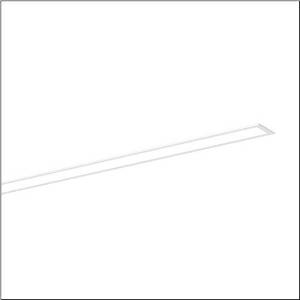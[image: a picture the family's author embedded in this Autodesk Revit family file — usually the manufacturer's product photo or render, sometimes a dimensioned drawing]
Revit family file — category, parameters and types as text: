
# Revit family: silica_r__21_51mx10tbt2w_f160
name_source: partatom
category: Lighting Fixtures
units: mm (PartAtom-declared; Revit-internal decimal feet)

## family parameters
Cut with Voids When Loaded = No
Host = Face
Light Source = No
Part Type = Normal
Room Calculation Point = No
Round Connector Dimension = Use Diameter
Shared = No

## types (1)
- --- (1 x LED, 3000 lm, 25.6 W, 6500K)
    Apparent Load = 26 VA
    CIE Flux Codes = 48 79 96 100 100
    Color Rendering = 80
    Color Temperature = 6500K
    Default Elevation = 1800 mm
    Description = Silica® 21, office luminaire, primary optical cover: cover, of PMMA, opal, light emission: direct distribution, primary light characteristic: symmetric, installation type: recessed, LED, rated luminous flux: 3.000lm, luminous efficacy: 112lm/W, light colour: 8tw, colour temperature: 2700..6500K, control gear: DALI DT8, with terminal, 3+2-pole, max. 2.5mm², mains connection: 220..240V, AC, 50/60Hz, rated input power: 26.9W, luminaire housing, of aluminium, traffic white (RAL 9016), length: 1.504mm, width: 77mm, height: 53mm, protection rating (complete): IP20, insulation class (complete): insulation class I (protective earthing), certification: CE, ENEC, VDE, permissible operating ambient temperature: 0..+35°C, standard: EN 50419, packaging unit: 1 piece
    Height = 0 mm  [stored 0 ft]
    Lamp = 1 x LED
    Lamp Light Flux = 3000 lm
    Lamp Power = 25.6 W
    Lamp count = 1
    Length = 1527 mm
    Luminous efficacy = 117 lm/W
    Manufacturer = Siteco
    ModVariant = No
    Model = 51MX10TBT2W
    Mounting Place = Ceiling
    Mounting Type = Recessed
    Number of Poles = 1
    OnlyDefault = Yes
    Power Factor = 1
    Product Name = Silica® 21
    Product group = office luminaire | ceiling recessed
    ProductGroupID = 401
    Protection Class = Protection class I
    Protection Degree = IP 20
    RLX_Detail_Level = 1
    RLX_Emergency_Light_Flux = 0 lm
    RLX_Emergency_Type = 0
    RLX_Emergency_Type_DB = No
    RlxData = <blob elided: 18021 chars, md5=e9ade9f5>
    Socket = socket
    Standby Power = 0 W
    System Light Flux = 3000 lm
    System Power = 26 W
    Type Comments = individual setting
    Type Image = l_1335891.jpg
    URL = http://relux.com
    VarID = @adj_139722
    Voltage = 0 V
    Weight = 0.00 kg
    Width = 79 mm

note: [stored X ft] marks values corroborated as IEEE doubles in the binary element streams (Revit-internal decimal feet)

## geometry (parser evidence)
native form markers: Blend x4, Sweep x9
no freeform markers — native parametric forms only
